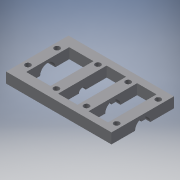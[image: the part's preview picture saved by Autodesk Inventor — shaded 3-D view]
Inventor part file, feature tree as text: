
AUTODESK INVENTOR PART (.ipt)
format: ipt  version: 2016 (Build 200138000, 138)  size: 219,648 bytes
history: native  units: mm
features: extrude x10, sketch x10, projected_geometry x1
ambient origin geometry x8: Origin, YZ Plane, XZ Plane, XY Plane, X Axis, Y Axis, Z Axis, Center Point
bodies: Solid1 (feature_tree)
feature tree (21):
  extrude  "Extrusion1"  Depth=28.0mm
  extrude  "Extrusion2"  Depth=70.0mm
  extrude  "Extrusion3"  Depth=15.0mm
  extrude  "Extrusion4"  Depth=10.0mm
  extrude  "Extrusion5"  Depth=15.0mm
  extrude  "Extrusion6"  Depth=7.0mm
  extrude  "Extrusion7"  Depth=7.0mm
  extrude  "Extrusion8"  Depth=7.0mm
  extrude  "Extrusion9"  Depth=7.0mm
  extrude  "Extrusion10"  Depth=10.0mm
  sketch  "Sketch1"  dims[d0=16.0mm d1=28.0mm]
  sketch  "Sketch2"  dims[d2=28.0mm d3=70.0mm]
  sketch  "Sketch3"  dims[d4=10.0mm d5=15.0mm]
  sketch  "Sketch4"  dims[d6=15.0mm d7=0.0mm d8=10.0mm]
  sketch  "Sketch5"  dims[d9=15.0mm d10=0.0mm d11=22.0mm]
  sketch  "Sketch6"  dims[d12=7.0mm d13=0.0mm d14=22.0mm]
  sketch  "Sketch7"  dims[d15=7.0mm d16=0.0mm d17=22.0mm]
  sketch  "Sketch8"  dims[d18=7.0mm d19=0.0mm d20=22.0mm]
  sketch  "Sketch9"  dims[d21=7.0mm d22=0.0mm d23=60.0mm]
  sketch  "Sketch10"  dims[d24=8.0mm d25=7.5mm d26=87.0mm d27=10.0mm d28=0.0mm d29=14.0mm d30=15.0mm d31=35.0mm d32=10.0mm d33=0.0mm d34=22.0mm d35=10.0mm d36=0.0mm d37=8.0mm d38=10.0mm d39=10.0mm d40=0.0mm]
  projected_geometry  "Projected Loop1"
